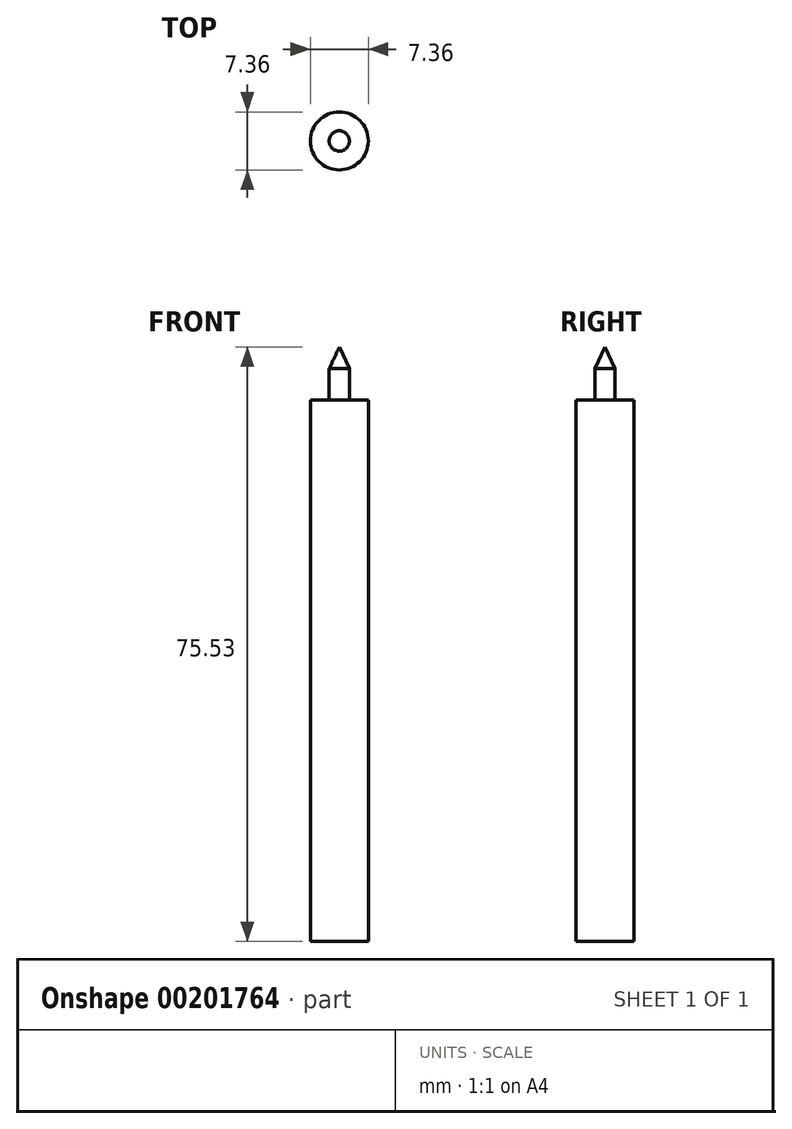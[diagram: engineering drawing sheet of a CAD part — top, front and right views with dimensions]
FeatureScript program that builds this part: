
annotation { "Feature Type Name" : "Feature", "Feature Type Description" : "" }
export const myFeature = defineFeature(function(context is Context, id is Id, definition is map)
    precondition{}
    {
        {
            var Q0;
            Q0=qCreatedBy(makeId("Front.planeOp"),FACE);
            var sketch = newSketch(context, id + "F0", { "sketchPlane" : qUnion([Q0])});
            skLineSegment(sketch, "E0", {"start": v(0, 75.53) * mm, "end": v(0, 0) * mm});
            skLineSegment(sketch, "E1", {"start": v(0, 0) * mm, "end": v(3.68, 0) * mm});
            skLineSegment(sketch, "E2", {"start": v(3.68, 0) * mm, "end": v(3.68, 68.78) * mm});
            skLineSegment(sketch, "E3", {"start": v(3.68, 68.78) * mm, "end": v(1.3, 68.78) * mm});
            skLineSegment(sketch, "E4", {"start": v(1.3, 68.78) * mm, "end": v(1.3, 72.77) * mm});
            skLineSegment(sketch, "E5", {"start": v(1.3, 72.77) * mm, "end": v(0, 75.53) * mm});
            skSolve(sketch);
        }
        {
            var Q0;
            Q0=makeQuery(id+"F0.imprint","IMPRINT",FACE,{"disambiguationData":[TD([[makeQuery(id+"F0.imprint","IMPRINT",EDGE,{"derivedFrom":sQuery(id+"F0.wireOp",EDGE,"E0")}),1.0]])]});
            var Q1;
            Q1=sQuery(id+"F0.wireOp",EDGE,"E0");
            revolve(context, id + "F1", {"entities" : qUnion([Q0]), "axis" : qUnion([Q1]), "revolveType" : RevolveType.FULL});
        }
    });
